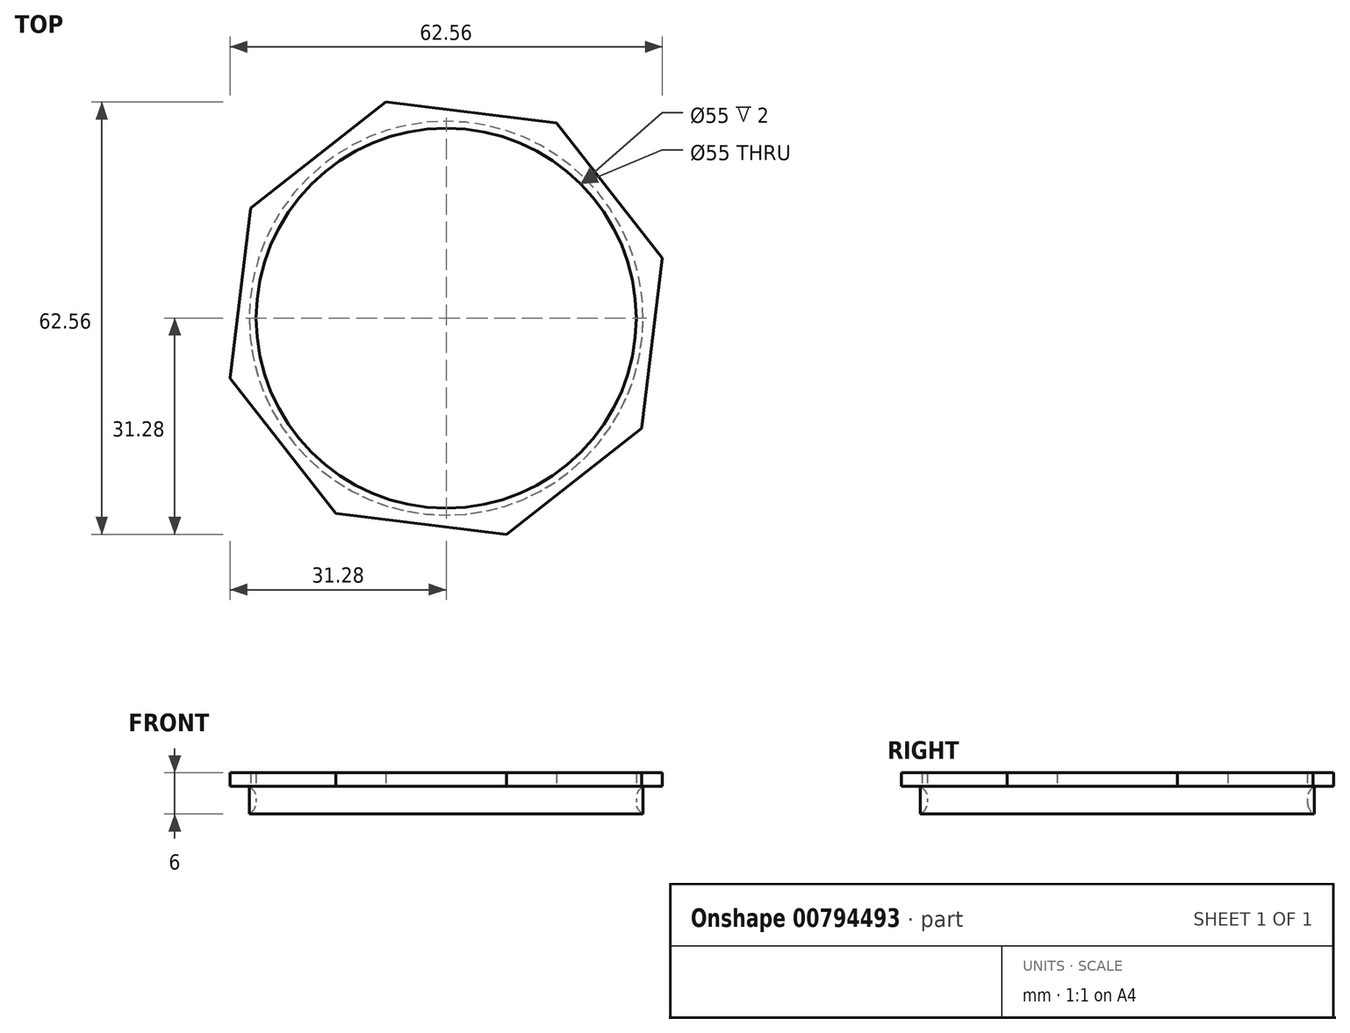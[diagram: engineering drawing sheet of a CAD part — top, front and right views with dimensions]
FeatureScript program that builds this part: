
annotation { "Feature Type Name" : "Feature", "Feature Type Description" : "" }
export const myFeature = defineFeature(function(context is Context, id is Id, definition is map)
    precondition{}
    {
        {
            var Q0;
            Q0=qCreatedBy(makeId("Top.planeOp"),FACE);
            var sketch = newSketch(context, id + "F0", { "sketchPlane" : qUnion([Q0])});
            skCircle(sketch, "E0", {"center": v(0, 0) * mm, "radius": 28.5 * mm});
            skCircle(sketch, "E1.cCircle", {"center": v(0, 0) * mm, "radius": 30 * mm, "construction": true});
            skLineSegment(sketch, "E1.0", {"start": v(28.28, -15.96) * mm, "end": v(8.7, -31.28) * mm});
            skLineSegment(sketch, "E1.1", {"start": v(8.7, -31.28) * mm, "end": v(-15.96, -28.28) * mm});
            skLineSegment(sketch, "E1.2", {"start": v(-15.96, -28.28) * mm, "end": v(-31.28, -8.7) * mm});
            skLineSegment(sketch, "E1.3", {"start": v(-31.28, -8.7) * mm, "end": v(-28.28, 15.96) * mm});
            skLineSegment(sketch, "E1.4", {"start": v(-28.28, 15.96) * mm, "end": v(-8.7, 31.28) * mm});
            skLineSegment(sketch, "E1.5", {"start": v(-8.7, 31.28) * mm, "end": v(15.96, 28.28) * mm});
            skLineSegment(sketch, "E1.6", {"start": v(15.96, 28.28) * mm, "end": v(31.28, 8.7) * mm});
            skLineSegment(sketch, "E1.7", {"start": v(31.28, 8.7) * mm, "end": v(28.28, -15.96) * mm});
            skPoint(sketch, "E1.0.midPoint", {"position": v(18.5, -23.62) * mm});
            skSolve(sketch);
        }
        {
            var Q0;
            Q0=makeQuery(id+"F0.imprint","IMPRINT",FACE,{"disambiguationData":[TD([[makeQuery(id+"F0.imprint","IMPRINT",EDGE,{"derivedFrom":sQuery(id+"F0.wireOp",EDGE,"E0")}),1.0]])]});
            extrude(context, id + "F1", {"entities" : qUnion([Q0]), "oppositeDirection" : true, "depth" : 4 * mm, "offsetDistance" : 25 * mm});
        }
        {
            var Q0;
            Q0 = qSketchRegion(id + "F0", true);
            var Q1;
            Q1=makeQuery(id+"F0.imprint","IMPRINT",FACE,{"disambiguationData":[TD([[makeQuery(id+"F0.imprint","IMPRINT",EDGE,{"derivedFrom":sQuery(id+"F0.wireOp",EDGE,"E0")}),1.0]])]});
            extrude(context, id + "F2", {"entities" : qUnion([Q0, Q1]), "depth" : 2 * mm, "offsetDistance" : 25 * mm});
        }
        {
            var Q0;
            Q0=makeQuery(id+"F1.opExtrude","CAP_FACE",FACE,{"disambiguationData":[OSD([sQuery(id+"F0.wireOp",EDGE,"E0")])],"isStart":false});
            var sketch = newSketch(context, id + "F3", { "sketchPlane" : qUnion([Q0])});
            skCircle(sketch, "E2", {"center": v(0, 0) * mm, "radius": 27.5 * mm});
            skSolve(sketch);
        }
        {
            var Q0;
            Q0=makeQuery(id+"F3.imprint","IMPRINT",FACE,{"disambiguationData":[TD([[makeQuery(id+"F3.imprint","IMPRINT",EDGE,{"derivedFrom":sQuery(id+"F3.wireOp",EDGE,"E2")}),1.0]])]});
            extrude(context, id + "F4", {"entities" : qUnion([Q0]), "operationType" : NewBodyOperationType.REMOVE, "oppositeDirection" : true, "depth" : 15 * mm, "offsetDistance" : 25 * mm});
        }
        {
            var Q0;
            Q0=makeQuery(id+"F4.boolean.opBoolean","INTERSECT",EDGE,{"derivedFrom":[makeQuery(id+"F1.opExtrude","CAP_FACE",FACE,{"disambiguationData":[OSD([sQuery(id+"F0.wireOp",EDGE,"E0")])],"isStart":true}),makeQuery(id+"F4.opExtrude","SWEPT_FACE",FACE,{"disambiguationData":[OSD([sQuery(id+"F3.wireOp",EDGE,"E2")])]})]});
            var Q1;
            Q1=makeQuery(id+"F4.boolean.opBoolean","COPY",FACE,{"derivedFrom":makeQuery(id+"F4.opExtrude","SWEPT_FACE",FACE,{"disambiguationData":[OSD([sQuery(id+"F3.wireOp",EDGE,"E2")])]})});
            fillet(context, id + "F5", {"entities" : qUnion([Q0, Q1]), "radius" : 2 * mm, "tangentPropagation" : true, "allowEdgeOverflow" : false});
        }
    });
